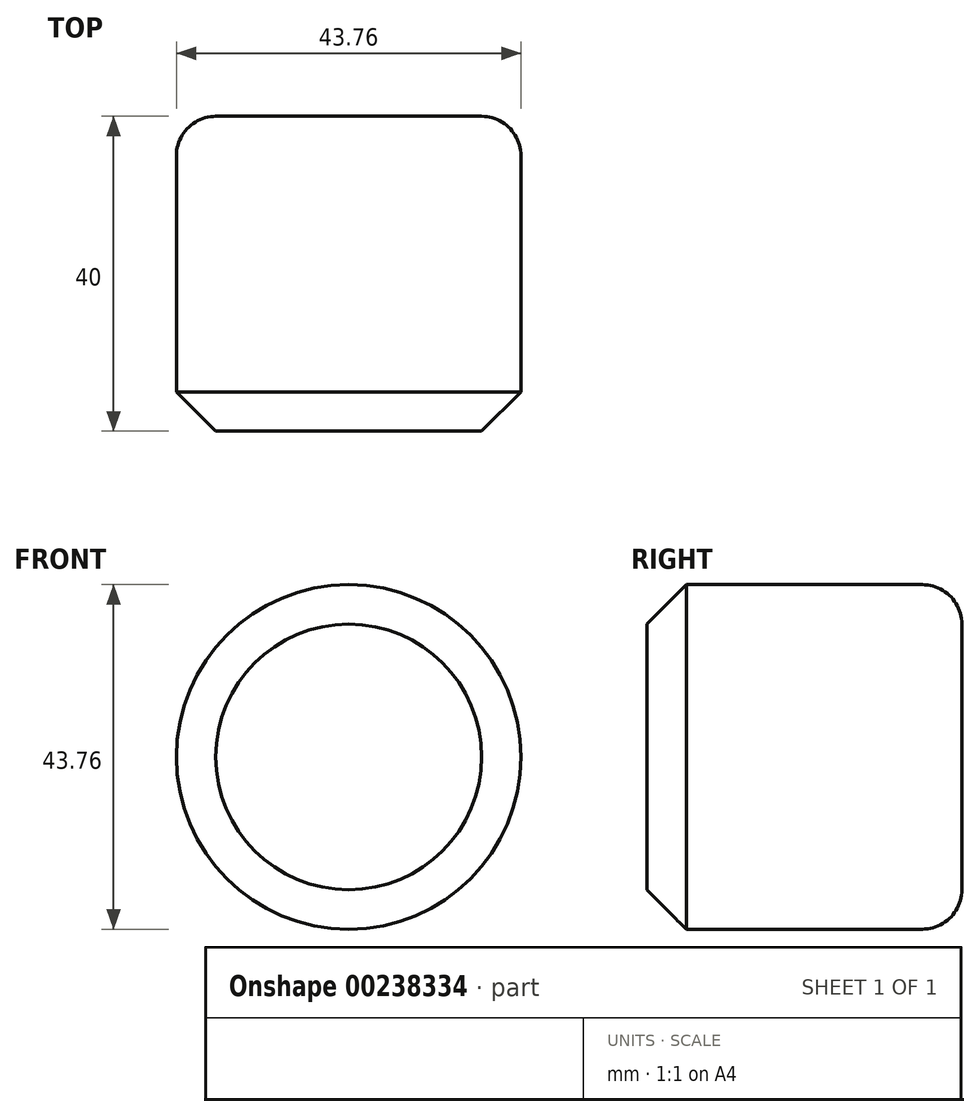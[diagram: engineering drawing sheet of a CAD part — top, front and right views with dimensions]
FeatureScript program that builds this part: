
annotation { "Feature Type Name" : "Feature", "Feature Type Description" : "" }
export const myFeature = defineFeature(function(context is Context, id is Id, definition is map)
    precondition{}
    {
        {
            var Q0;
            Q0=qCreatedBy(makeId("Front.planeOp"),FACE);
            var sketch = newSketch(context, id + "F0", { "sketchPlane" : qUnion([Q0])});
            skCircle(sketch, "E0", {"center": v(0, 0) * mm, "radius": 21.88 * mm});
            skSolve(sketch);
        }
        {
            var Q0;
            Q0 = qSketchRegion(id + "F0", true);
            extrude(context, id + "F1", {"entities" : qUnion([Q0]), "depth" : 40 * mm});
        }
        {
            var Q0;
            Q0=makeQuery(id+"F1.opExtrude","CAP_EDGE",EDGE,{"disambiguationData":[OSD([sQuery(id+"F0.wireOp",EDGE,"E0")])],"isStart":false});
            chamfer(context, id + "F2", {"entities" : qUnion([Q0]), "width" : 5 * mm, "tangentPropagation" : true});
        }
        {
            var Q0;
            Q0=makeQuery(id+"F1.opExtrude","CAP_EDGE",EDGE,{"disambiguationData":[OSD([sQuery(id+"F0.wireOp",EDGE,"E0")])],"isStart":true});
            fillet(context, id + "F3", {"entities" : qUnion([Q0]), "radius" : 5 * mm, "tangentPropagation" : true, "allowEdgeOverflow" : false});
        }
    });
